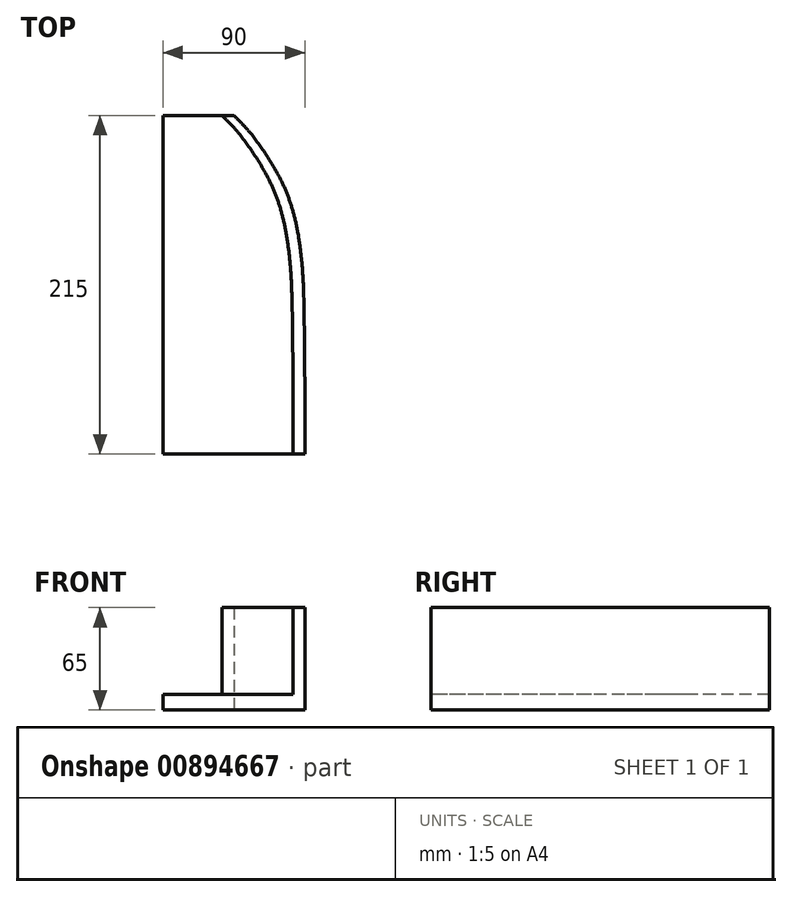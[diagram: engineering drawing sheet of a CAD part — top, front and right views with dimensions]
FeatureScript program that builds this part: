
annotation { "Feature Type Name" : "Feature", "Feature Type Description" : "" }
export const myFeature = defineFeature(function(context is Context, id is Id, definition is map)
    precondition{}
    {
        {
            var Q0;
            Q0=qCreatedBy(makeId("Top.planeOp"),FACE);
            var sketch = newSketch(context, id + "F0", { "sketchPlane" : qUnion([Q0])});
            skLineSegment(sketch, "E0.bottom", {"start": v(-43.92, 85.1) * mm, "end": v(46.08, 85.1) * mm});
            skLineSegment(sketch, "E0.top", {"start": v(-43.92, -129.9) * mm, "end": v(46.08, -129.9) * mm});
            skLineSegment(sketch, "E0.left", {"start": v(-43.92, 85.1) * mm, "end": v(-43.92, -129.9) * mm});
            skLineSegment(sketch, "E0.right", {"start": v(46.08, 85.1) * mm, "end": v(46.08, -129.9) * mm});
            skLineSegment(sketch, "E1", {"start": v(1.08, 85.1) * mm, "end": v(-43.92, 85.1) * mm});
            skLineSegment(sketch, "E2", {"start": v(46.08, -129.9) * mm, "end": v(46.08, -84.9) * mm});
            skFitSpline(sketch, "E3", {"points": [v(46.08, -84.9) * mm, v(45.32, -27.72) * mm, v(44.1, -7.22) * mm, v(41.09, 13.8) * mm, v(35.92, 32.5) * mm, v(27.14, 51.19) * mm, v(11.79, 73.73) * mm, v(1.08, 85.1) * mm], "startDerivative": vector(-2.3, 298.4) * mm, "endDerivative": vector(-90.29, 88.1) * mm});
            skLineSegment(sketch, "E4", {"start": v(35.92, 32.5) * mm, "end": v(28.42, 32.5) * mm});
            skLineSegment(sketch, "E5", {"start": v(41.09, 13.8) * mm, "end": v(33.59, 13.8) * mm});
            skLineSegment(sketch, "E6", {"start": v(44.1, -7.22) * mm, "end": v(36.6, -7.22) * mm});
            skLineSegment(sketch, "E7", {"start": v(45.32, -27.72) * mm, "end": v(37.82, -27.72) * mm});
            skLineSegment(sketch, "E8", {"start": v(46.08, -84.9) * mm, "end": v(38.58, -84.9) * mm});
            skLineSegment(sketch, "E9", {"start": v(46.08, -129.9) * mm, "end": v(38.58, -129.9) * mm});
            skLineSegment(sketch, "E10", {"start": v(11.79, 73.73) * mm, "end": v(46.08, 73.73) * mm});
            skLineSegment(sketch, "E11", {"start": v(27.14, 51.19) * mm, "end": v(46.08, 51.19) * mm});
            skLineSegment(sketch, "E12", {"start": v(11.79, 73.73) * mm, "end": v(4.29, 73.73) * mm});
            skLineSegment(sketch, "E13", {"start": v(27.14, 51.19) * mm, "end": v(19.64, 51.19) * mm});
            skLineSegment(sketch, "E14", {"start": v(1.08, 85.1) * mm, "end": v(-6.42, 85.1) * mm});
            skFitSpline(sketch, "E15", {"points": [v(-6.42, 85.1) * mm, v(4.29, 73.73) * mm, v(19.64, 51.19) * mm, v(28.42, 32.5) * mm, v(33.59, 13.8) * mm, v(36.6, -7.22) * mm, v(37.82, -27.72) * mm, v(38.58, -84.9) * mm, v(38.58, -129.9) * mm], "startDerivative": vector(107.89, -105) * mm, "endDerivative": vector(-0.73, -258.71) * mm});
            skSolve(sketch);
        }
        {
            var Q0;
            {var subQ1=sQuery(id+"F0.wireOp",EDGE,"E0.top");Q0=makeQuery(id+"F0.imprint","IMPRINT",FACE,{"disambiguationData":[TD([[makeQuery(id+"F0.imprint","IMPRINT",EDGE,{"derivedFrom":subQ1}),1.0]])]});}
            extrude(context, id + "F1", {"entities" : qUnion([Q0]), "depth" : 10 * mm, "offsetDistance" : 25 * mm});
        }
        {
            var Q0;
            {var subQ7=sQuery(id+"F0.wireOp",EDGE,"E0.left");Q0=makeQuery(id+"F0.imprint","IMPRINT",FACE,{"disambiguationData":[TD([[makeQuery(id+"F0.imprint","IMPRINT",EDGE,{"derivedFrom":subQ7}),1.0]])]});}
            var Q1;
            {var subQ5=sQuery(id+"F0.wireOp",EDGE,"E12");Q1=makeQuery(id+"F0.imprint","IMPRINT",FACE,{"disambiguationData":[TD([[makeQuery(id+"F0.imprint","IMPRINT",EDGE,{"derivedFrom":subQ5}),-1.0]])]});}
            var Q2;
            {var subQ0=sQuery(id+"F0.wireOp",EDGE,"E12");Q2=makeQuery(id+"F0.imprint","IMPRINT",FACE,{"disambiguationData":[TD([[makeQuery(id+"F0.imprint","IMPRINT",EDGE,{"derivedFrom":subQ0}),1.0]])]});}
            var Q3;
            {var subQ0=sQuery(id+"F0.wireOp",EDGE,"E4");Q3=makeQuery(id+"F0.imprint","IMPRINT",FACE,{"disambiguationData":[TD([[makeQuery(id+"F0.imprint","IMPRINT",EDGE,{"derivedFrom":subQ0}),-1.0]])]});}
            var Q4;
            {var subQ0=sQuery(id+"F0.wireOp",EDGE,"E4");Q4=makeQuery(id+"F0.imprint","IMPRINT",FACE,{"disambiguationData":[TD([[makeQuery(id+"F0.imprint","IMPRINT",EDGE,{"derivedFrom":subQ0}),1.0]])]});}
            var Q5;
            {var subQ0=sQuery(id+"F0.wireOp",EDGE,"E5");Q5=makeQuery(id+"F0.imprint","IMPRINT",FACE,{"disambiguationData":[TD([[makeQuery(id+"F0.imprint","IMPRINT",EDGE,{"derivedFrom":subQ0}),1.0]])]});}
            var Q6;
            {var subQ0=sQuery(id+"F0.wireOp",EDGE,"E6");Q6=makeQuery(id+"F0.imprint","IMPRINT",FACE,{"disambiguationData":[TD([[makeQuery(id+"F0.imprint","IMPRINT",EDGE,{"derivedFrom":subQ0}),1.0]])]});}
            var Q7;
            {var subQ2=sQuery(id+"F0.wireOp",EDGE,"E7");Q7=makeQuery(id+"F0.imprint","IMPRINT",FACE,{"disambiguationData":[TD([[makeQuery(id+"F0.imprint","IMPRINT",EDGE,{"derivedFrom":subQ2}),1.0]])]});}
            extrude(context, id + "F2", {"entities" : qUnion([Q0, Q1, Q2, Q3, Q4, Q5, Q6, Q7]), "operationType" : NewBodyOperationType.ADD, "depth" : 10 * mm, "offsetDistance" : 25 * mm});
        }
        {
            var Q0;
            {var subQ5=sQuery(id+"F0.wireOp",EDGE,"E8");Q0=makeQuery(id+"F0.imprint","IMPRINT",FACE,{"disambiguationData":[TD([[makeQuery(id+"F0.imprint","IMPRINT",EDGE,{"derivedFrom":subQ5}),1.0]])]});}
            var Q1;
            {var subQ2=sQuery(id+"F0.wireOp",EDGE,"E7");Q1=makeQuery(id+"F0.imprint","IMPRINT",FACE,{"disambiguationData":[TD([[makeQuery(id+"F0.imprint","IMPRINT",EDGE,{"derivedFrom":subQ2}),1.0]])]});}
            var Q2;
            {var subQ0=sQuery(id+"F0.wireOp",EDGE,"E6");Q2=makeQuery(id+"F0.imprint","IMPRINT",FACE,{"disambiguationData":[TD([[makeQuery(id+"F0.imprint","IMPRINT",EDGE,{"derivedFrom":subQ0}),1.0]])]});}
            var Q3;
            {var subQ0=sQuery(id+"F0.wireOp",EDGE,"E5");Q3=makeQuery(id+"F0.imprint","IMPRINT",FACE,{"disambiguationData":[TD([[makeQuery(id+"F0.imprint","IMPRINT",EDGE,{"derivedFrom":subQ0}),1.0]])]});}
            var Q4;
            {var subQ0=sQuery(id+"F0.wireOp",EDGE,"E4");Q4=makeQuery(id+"F0.imprint","IMPRINT",FACE,{"disambiguationData":[TD([[makeQuery(id+"F0.imprint","IMPRINT",EDGE,{"derivedFrom":subQ0}),1.0]])]});}
            var Q5;
            {var subQ0=sQuery(id+"F0.wireOp",EDGE,"E4");Q5=makeQuery(id+"F0.imprint","IMPRINT",FACE,{"disambiguationData":[TD([[makeQuery(id+"F0.imprint","IMPRINT",EDGE,{"derivedFrom":subQ0}),-1.0]])]});}
            var Q6;
            {var subQ5=sQuery(id+"F0.wireOp",EDGE,"E12");Q6=makeQuery(id+"F0.imprint","IMPRINT",FACE,{"disambiguationData":[TD([[makeQuery(id+"F0.imprint","IMPRINT",EDGE,{"derivedFrom":subQ5}),-1.0]])]});}
            var Q7;
            {var subQ0=sQuery(id+"F0.wireOp",EDGE,"E12");Q7=makeQuery(id+"F0.imprint","IMPRINT",FACE,{"disambiguationData":[TD([[makeQuery(id+"F0.imprint","IMPRINT",EDGE,{"derivedFrom":subQ0}),1.0]])]});}
            extrude(context, id + "F3", {"entities" : qUnion([Q0, Q1, Q2, Q3, Q4, Q5, Q6, Q7]), "operationType" : NewBodyOperationType.ADD, "depth" : 65 * mm, "offsetDistance" : 25 * mm});
        }
    });
